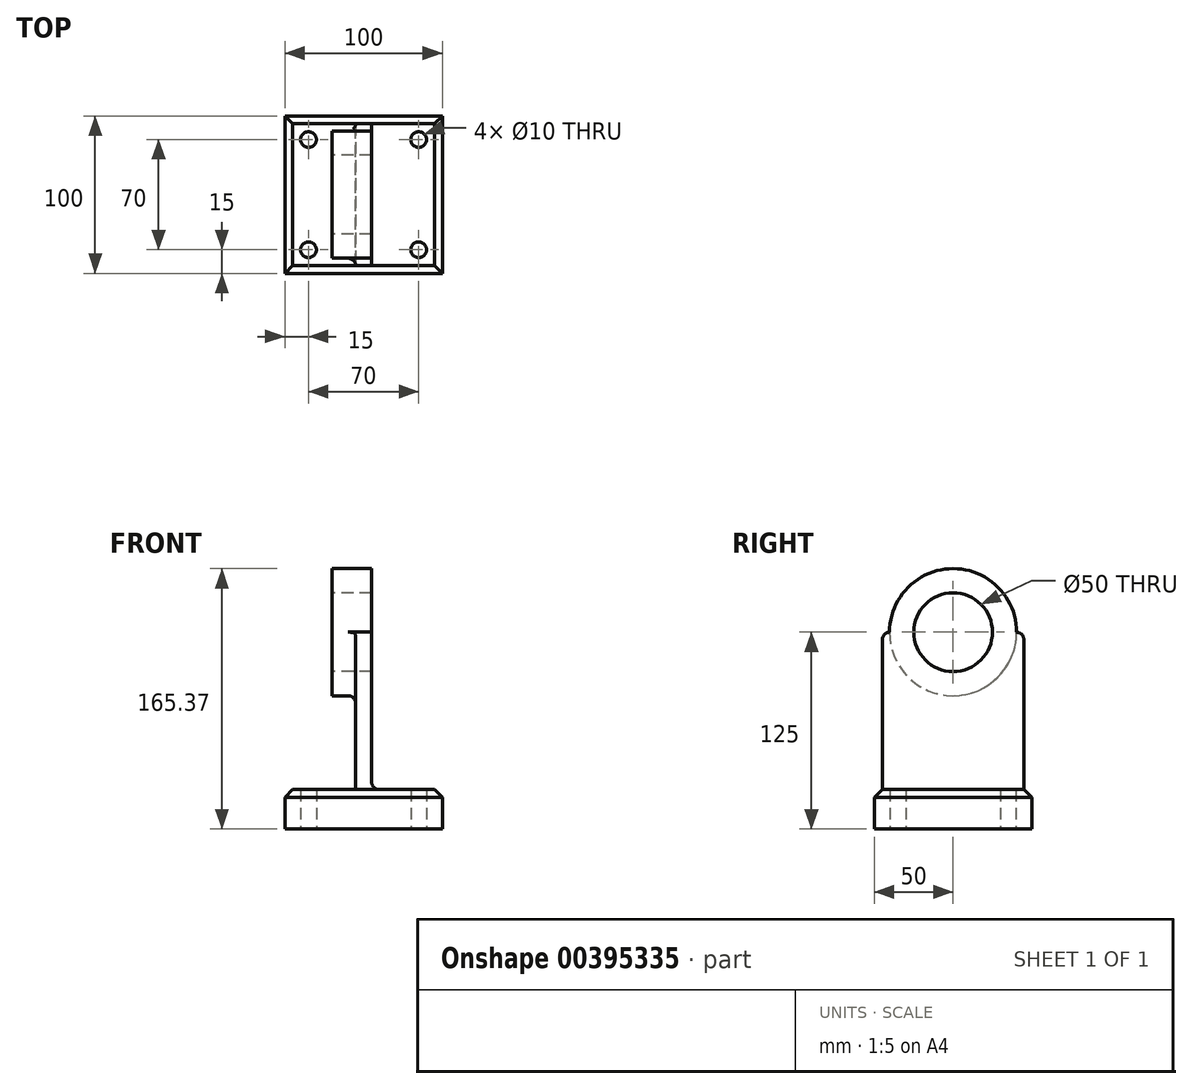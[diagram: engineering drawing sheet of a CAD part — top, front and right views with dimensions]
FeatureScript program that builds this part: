
annotation { "Feature Type Name" : "Feature", "Feature Type Description" : "" }
export const myFeature = defineFeature(function(context is Context, id is Id, definition is map)
    precondition{}
    {
        {
            var Q0;
            Q0=qCreatedBy(makeId("Top.planeOp"),FACE);
            var sketch = newSketch(context, id + "F0", { "sketchPlane" : qUnion([Q0])});
            skLineSegment(sketch, "E0.bottom", {"start": v(-50, 50) * mm, "end": v(50, 50) * mm});
            skLineSegment(sketch, "E0.top", {"start": v(-50, -50) * mm, "end": v(50, -50) * mm});
            skLineSegment(sketch, "E0.left", {"start": v(-50, 50) * mm, "end": v(-50, -50) * mm});
            skLineSegment(sketch, "E0.right", {"start": v(50, 50) * mm, "end": v(50, -50) * mm});
            skPoint(sketch, "E0.middle", {"position": v(0, 0) * mm});
            skSolve(sketch);
        }
        {
            var Q0;
            Q0=makeQuery(id+"F0.imprint","IMPRINT",FACE,{"disambiguationData":[TD([[makeQuery(id+"F0.imprint","IMPRINT",EDGE,{"derivedFrom":sQuery(id+"F0.wireOp",EDGE,"E0.bottom")}),-1.0]])]});
            extrude(context, id + "F1", {"entities" : qUnion([Q0]), "depth" : 25 * mm});
        }
        {
            var Q0;
            Q0=makeQuery(id+"F1.opExtrude","CAP_EDGE",EDGE,{"disambiguationData":[OSD([sQuery(id+"F0.wireOp",EDGE,"E0.top")])],"isStart":false});
            var Q1;
            Q1=makeQuery(id+"F1.opExtrude","CAP_EDGE",EDGE,{"disambiguationData":[OSD([sQuery(id+"F0.wireOp",EDGE,"E0.right")])],"isStart":false});
            var Q2;
            Q2=makeQuery(id+"F1.opExtrude","CAP_EDGE",EDGE,{"disambiguationData":[OSD([sQuery(id+"F0.wireOp",EDGE,"E0.left")])],"isStart":false});
            var Q3;
            Q3=makeQuery(id+"F1.opExtrude","CAP_EDGE",EDGE,{"disambiguationData":[OSD([sQuery(id+"F0.wireOp",EDGE,"E0.bottom")])],"isStart":false});
            chamfer(context, id + "F2", {"entities" : qUnion([Q0, Q1, Q2, Q3]), "width" : 5 * mm, "tangentPropagation" : true});
        }
        {
            var Q0;
            Q0=makeQuery(id+"F1.opExtrude","CAP_FACE",FACE,{"disambiguationData":[OSD([sQuery(id+"F0.wireOp",EDGE,"E0.bottom"),sQuery(id+"F0.wireOp",EDGE,"E0.top"),sQuery(id+"F0.wireOp",EDGE,"E0.left"),sQuery(id+"F0.wireOp",EDGE,"E0.right")])],"isStart":false});
            var sketch = newSketch(context, id + "F3", { "sketchPlane" : qUnion([Q0])});
            skLineSegment(sketch, "E1.bottom", {"start": v(-5, 45) * mm, "end": v(5, 45) * mm});
            skLineSegment(sketch, "E1.top", {"start": v(-5, -45) * mm, "end": v(5, -45) * mm});
            skLineSegment(sketch, "E1.left", {"start": v(-5, 45) * mm, "end": v(-5, -45) * mm});
            skLineSegment(sketch, "E1.right", {"start": v(5, 45) * mm, "end": v(5, -45) * mm});
            skPoint(sketch, "E1.middle", {"position": v(0, 0) * mm});
            skSolve(sketch);
        }
        {
            var Q0;
            Q0=makeQuery(id+"F3.imprint","IMPRINT",FACE,{"disambiguationData":[TD([[makeQuery(id+"F3.imprint","IMPRINT",EDGE,{"derivedFrom":sQuery(id+"F3.wireOp",EDGE,"E1.bottom")}),1.0]])]});
            extrude(context, id + "F4", {"entities" : qUnion([Q0]), "operationType" : NewBodyOperationType.ADD, "depth" : 100 * mm});
        }
        {
            var Q0;
            Q0=makeQuery(id+"F4.opExtrude","CAP_EDGE",EDGE,{"disambiguationData":[OSD([sQuery(id+"F3.wireOp",EDGE,"E1.top")])],"isStart":false});
            var Q1;
            Q1=makeQuery(id+"F4.opExtrude","CAP_EDGE",EDGE,{"disambiguationData":[OSD([sQuery(id+"F3.wireOp",EDGE,"E1.bottom")])],"isStart":false});
            fillet(context, id + "F5", {"entities" : qUnion([Q0, Q1]), "radius" : 5 * mm, "tangentPropagation" : true, "allowEdgeOverflow" : false});
        }
        {
            var Q0;
            Q0=makeQuery(id+"F4.opExtrude","SWEPT_FACE",FACE,{"disambiguationData":[OSD([sQuery(id+"F3.wireOp",EDGE,"E1.right")])]});
            var sketch = newSketch(context, id + "F6", { "sketchPlane" : qUnion([Q0])});
            skCircle(sketch, "E2", {"center": v(0, 125) * mm, "radius": 40.37 * mm});
            skSolve(sketch);
        }
        {
            var Q0;
            {var subQ1=sQuery(id+"F3.wireOp",EDGE,"E1.right");var subQ7=makeQuery(id+"F4.opExtrude","CAP_EDGE",EDGE,{"disambiguationData":[OSD([subQ1])],"isStart":false});Q0=makeQuery(id+"F6.imprint","IMPRINT",FACE,{"disambiguationData":[TD([[makeQuery(id+"F6.imprint","IMPRINT",EDGE,{"derivedFrom":subQ7}),-1.0]])]});}
            var Q1;
            {var subQ1=sQuery(id+"F3.wireOp",EDGE,"E1.right");var subQ7=makeQuery(id+"F4.opExtrude","CAP_EDGE",EDGE,{"disambiguationData":[OSD([subQ1])],"isStart":false});Q1=makeQuery(id+"F6.imprint","IMPRINT",FACE,{"disambiguationData":[TD([[makeQuery(id+"F6.imprint","IMPRINT",EDGE,{"derivedFrom":subQ7}),1.0]])]});}
            extrude(context, id + "F7", {"entities" : qUnion([Q0, Q1]), "operationType" : NewBodyOperationType.ADD, "oppositeDirection" : true, "depth" : 25 * mm});
        }
        {
            var Q0;
            Q0=makeQuery(id+"F7.opExtrude","CAP_FACE",FACE,{"disambiguationData":[OSD([sQuery(id+"F6.wireOp",EDGE,"E2")])],"isStart":false});
            var sketch = newSketch(context, id + "F8", { "sketchPlane" : qUnion([Q0])});
            skCircle(sketch, "E3", {"center": v(0, 125) * mm, "radius": 30.27 * mm});
            skSolve(sketch);
        }
        {
            var Q0;
            Q0=sQuery(id+"F8.wireOp",VERTEX,"E3.center");
            var Q1;
            Q1=makeQuery(id+"F1.opExtrude","SWEPT_BODY",BODY,{"disambiguationData":[OSD([sQuery(id+"F0.wireOp",EDGE,"E0.bottom"),sQuery(id+"F0.wireOp",EDGE,"E0.top"),sQuery(id+"F0.wireOp",EDGE,"E0.left"),sQuery(id+"F0.wireOp",EDGE,"E0.right")])]});
            hole(context, id + "F9", {"style" : HoleStyle.SIMPLE, "endStyle" : HoleEndStyle.THROUGH, "holeDiameter" : 50 * mm, "isTappedThrough" : true, "tappedDepth" : 12 * mm, "tapClearance" : 3, "locations" : qUnion([Q0]), "scope" : qUnion([Q1])});
        }
        {
            var Q0;
            Q0=makeQuery(id+"F4.opExtrude","CAP_EDGE",EDGE,{"disambiguationData":[OSD([sQuery(id+"F3.wireOp",EDGE,"E1.right")])],"isStart":true});
            var Q1;
            Q1=makeQuery(id+"F4.opExtrude","CAP_EDGE",EDGE,{"disambiguationData":[OSD([sQuery(id+"F3.wireOp",EDGE,"E1.left")])],"isStart":true});
            fillet(context, id + "F10", {"entities" : qUnion([Q0, Q1]), "radius" : 5 * mm, "tangentPropagation" : true, "allowEdgeOverflow" : false});
        }
        {
            var Q0;
            Q0=makeQuery(id+"F1.opExtrude","CAP_FACE",FACE,{"disambiguationData":[OSD([sQuery(id+"F0.wireOp",EDGE,"E0.bottom"),sQuery(id+"F0.wireOp",EDGE,"E0.top"),sQuery(id+"F0.wireOp",EDGE,"E0.left"),sQuery(id+"F0.wireOp",EDGE,"E0.right")])],"isStart":true});
            var sketch = newSketch(context, id + "F11", { "sketchPlane" : qUnion([Q0])});
            skLineSegment(sketch, "E4.bottom", {"start": v(-35, 35) * mm, "end": v(35, 35) * mm});
            skLineSegment(sketch, "E4.top", {"start": v(-35, -35) * mm, "end": v(35, -35) * mm});
            skLineSegment(sketch, "E4.left", {"start": v(-35, 35) * mm, "end": v(-35, -35) * mm});
            skLineSegment(sketch, "E4.right", {"start": v(35, 35) * mm, "end": v(35, -35) * mm});
            skPoint(sketch, "E4.middle", {"position": v(0, 0) * mm});
            skSolve(sketch);
        }
        {
            var Q0;
            Q0=sQuery(id+"F11.wireOp",VERTEX,"E4.bottom.start");
            var Q1;
            Q1=sQuery(id+"F11.wireOp",VERTEX,"E4.left.end");
            var Q2;
            Q2=sQuery(id+"F11.wireOp",VERTEX,"E4.right.end");
            var Q3;
            Q3=sQuery(id+"F11.wireOp",VERTEX,"E4.right.start");
            var Q4;
            Q4=makeQuery(id+"F1.opExtrude","SWEPT_BODY",BODY,{"disambiguationData":[OSD([sQuery(id+"F0.wireOp",EDGE,"E0.bottom"),sQuery(id+"F0.wireOp",EDGE,"E0.top"),sQuery(id+"F0.wireOp",EDGE,"E0.left"),sQuery(id+"F0.wireOp",EDGE,"E0.right")])]});
            hole(context, id + "F12", {"style" : HoleStyle.SIMPLE, "endStyle" : HoleEndStyle.THROUGH, "holeDiameter" : 10 * mm, "isTappedThrough" : true, "tappedDepth" : 12 * mm, "tapClearance" : 3, "locations" : qUnion([Q0, Q1, Q2, Q3]), "scope" : qUnion([Q4])});
        }
        {
            var Q0;
            Q0=makeQuery(id+"F7.boolean.opBoolean","INTERSECT",EDGE,{"derivedFrom":[makeQuery(id+"F4.opExtrude","SWEPT_FACE",FACE,{"disambiguationData":[OSD([sQuery(id+"F3.wireOp",EDGE,"E1.left")])]}),makeQuery(id+"F7.opExtrude","SWEPT_FACE",FACE,{"disambiguationData":[OSD([sQuery(id+"F6.wireOp",EDGE,"E2")])]})]});
            fillet(context, id + "F13", {"entities" : qUnion([Q0]), "radius" : 5 * mm, "tangentPropagation" : true, "allowEdgeOverflow" : false});
        }
    });
